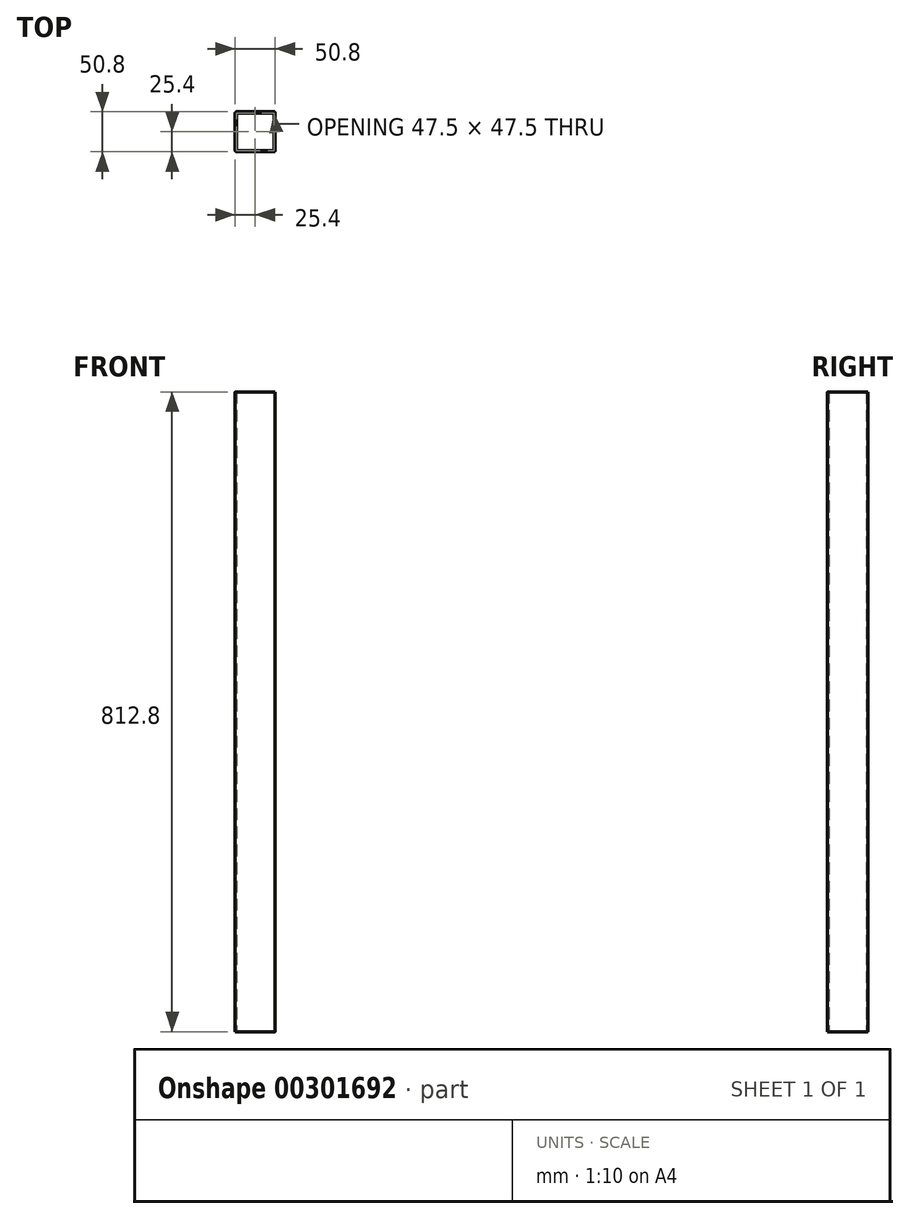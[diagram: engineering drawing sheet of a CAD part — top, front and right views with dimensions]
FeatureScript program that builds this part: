
annotation { "Feature Type Name" : "Feature", "Feature Type Description" : "" }
export const myFeature = defineFeature(function(context is Context, id is Id, definition is map)
    precondition{}
    {
        {
            var Q0;
            Q0=qCreatedBy(makeId("Top.planeOp"),FACE);
            var sketch = newSketch(context, id + "F0", { "sketchPlane" : qUnion([Q0])});
            skLineSegment(sketch, "E0.bottom", {"start": v(23.75, -25.4) * mm, "end": v(-23.75, -25.4) * mm});
            skLineSegment(sketch, "E0.top", {"start": v(23.75, 25.4) * mm, "end": v(-23.75, 25.4) * mm});
            skLineSegment(sketch, "E0.left", {"start": v(25.4, -23.75) * mm, "end": v(25.4, 23.75) * mm});
            skLineSegment(sketch, "E0.right", {"start": v(-25.4, -23.75) * mm, "end": v(-25.4, 23.75) * mm});
            skPoint(sketch, "E0.middle", {"position": v(0, 0) * mm});
            skLineSegment(sketch, "E1.0", {"start": v(22.1, 23.75) * mm, "end": v(-22.1, 23.75) * mm});
            skLineSegment(sketch, "E1.1", {"start": v(23.75, -22.1) * mm, "end": v(23.75, 22.1) * mm});
            skLineSegment(sketch, "E1.2", {"start": v(22.1, -23.75) * mm, "end": v(-22.1, -23.75) * mm});
            skLineSegment(sketch, "E1.3", {"start": v(-23.75, -22.1) * mm, "end": v(-23.75, 22.1) * mm});
            skPoint(sketch, "E2.visualSharp", {"position": v(-23.75, 23.75) * mm});
            skArc(sketch, "E2.filletArc", {"start": v(-22.1, 23.75) * mm, "mid": v(-23.27, 23.27) * mm, "end": v(-23.75, 22.1) * mm});
            skPoint(sketch, "E3.visualSharp", {"position": v(23.75, 23.75) * mm});
            skArc(sketch, "E3.filletArc", {"start": v(23.75, 22.1) * mm, "mid": v(23.27, 23.27) * mm, "end": v(22.1, 23.75) * mm});
            skPoint(sketch, "E4.visualSharp", {"position": v(23.75, -23.75) * mm});
            skArc(sketch, "E4.filletArc", {"start": v(22.1, -23.75) * mm, "mid": v(23.27, -23.27) * mm, "end": v(23.75, -22.1) * mm});
            skPoint(sketch, "E5.visualSharp", {"position": v(-23.75, -23.75) * mm});
            skArc(sketch, "E5.filletArc", {"start": v(-23.75, -22.1) * mm, "mid": v(-23.27, -23.27) * mm, "end": v(-22.1, -23.75) * mm});
            skPoint(sketch, "E6.visualSharp", {"position": v(-25.4, -25.4) * mm});
            skArc(sketch, "E6.filletArc", {"start": v(-25.4, -23.75) * mm, "mid": v(-24.92, -24.92) * mm, "end": v(-23.75, -25.4) * mm});
            skPoint(sketch, "E7.visualSharp", {"position": v(-25.4, 25.4) * mm});
            skArc(sketch, "E7.filletArc", {"start": v(-23.75, 25.4) * mm, "mid": v(-24.92, 24.92) * mm, "end": v(-25.4, 23.75) * mm});
            skPoint(sketch, "E8.visualSharp", {"position": v(25.4, 25.4) * mm});
            skArc(sketch, "E8.filletArc", {"start": v(25.4, 23.75) * mm, "mid": v(24.92, 24.92) * mm, "end": v(23.75, 25.4) * mm});
            skPoint(sketch, "E9.visualSharp", {"position": v(25.4, -25.4) * mm});
            skArc(sketch, "E9.filletArc", {"start": v(23.75, -25.4) * mm, "mid": v(24.92, -24.92) * mm, "end": v(25.4, -23.75) * mm});
            skSolve(sketch);
        }
        {
            var Q0;
            Q0=makeQuery(id+"F0.imprint","IMPRINT",FACE,{"disambiguationData":[TD([[makeQuery(id+"F0.imprint","IMPRINT",EDGE,{"derivedFrom":sQuery(id+"F0.wireOp",EDGE,"E0.bottom")}),-1.0]])]});
            extrude(context, id + "F1", {"entities" : qUnion([Q0]), "depth" : 812.8 * mm});
        }
    });
